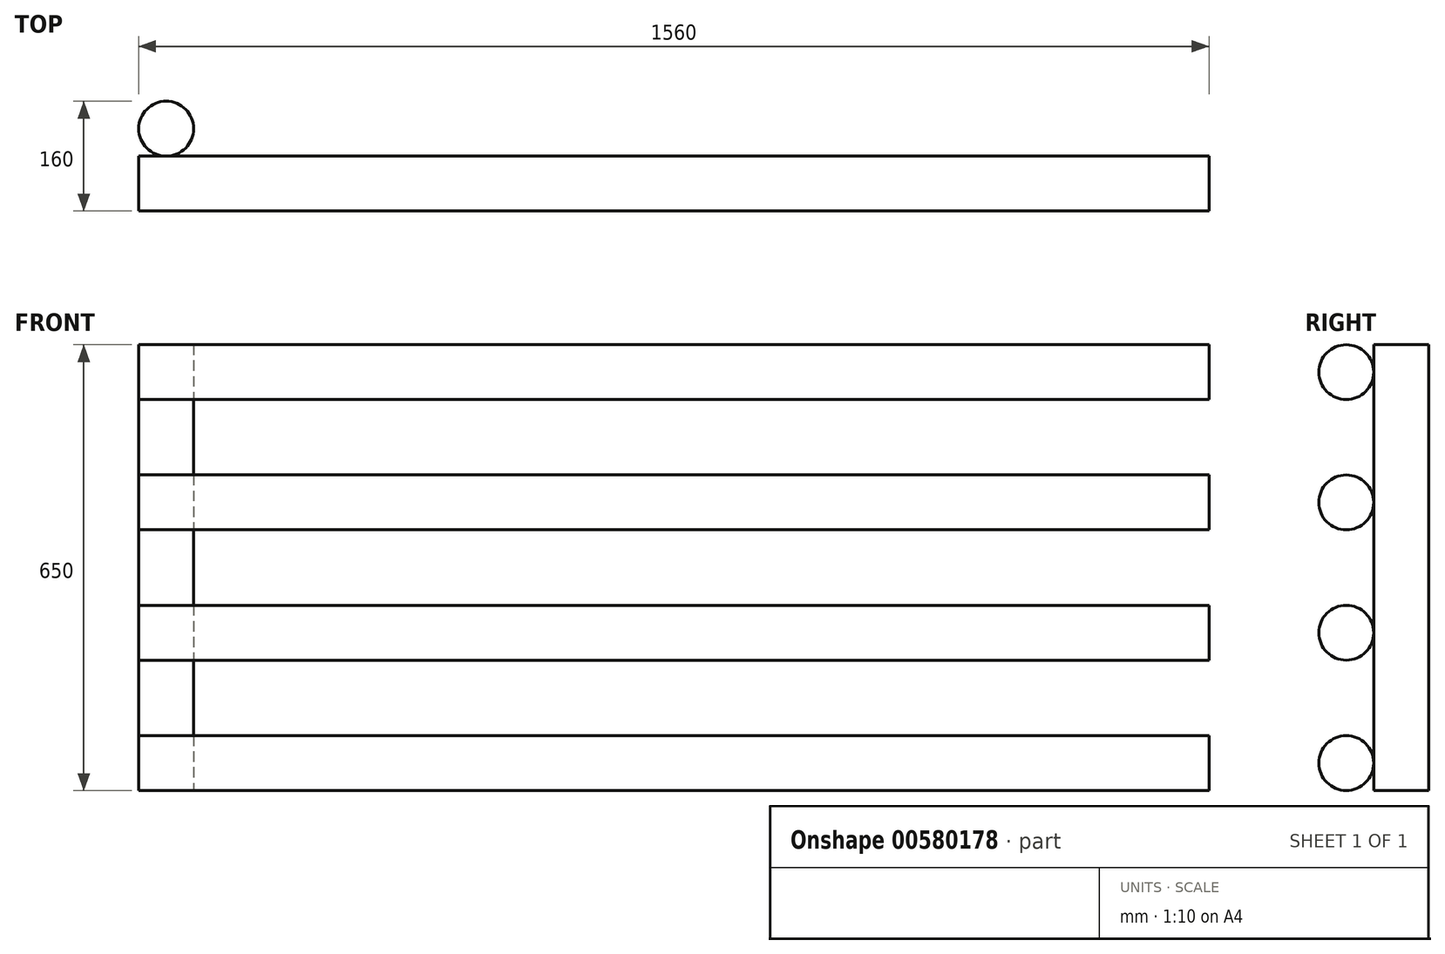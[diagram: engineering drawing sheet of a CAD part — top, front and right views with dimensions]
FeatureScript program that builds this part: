
annotation { "Feature Type Name" : "Feature", "Feature Type Description" : "" }
export const myFeature = defineFeature(function(context is Context, id is Id, definition is map)
    precondition{}
    {
        {
            var Q0;
            Q0=qCreatedBy(makeId("Right.planeOp"),FACE);
            var sketch = newSketch(context, id + "F0", { "sketchPlane" : qUnion([Q0])});
            skCircle(sketch, "E0", {"center": v(0, 0) * mm, "radius": 40 * mm});
            skCircle(sketch, "E1", {"center": v(0, 190) * mm, "radius": 40 * mm});
            skCircle(sketch, "E2", {"center": v(0, 380) * mm, "radius": 40 * mm});
            skCircle(sketch, "E3", {"center": v(0, 570) * mm, "radius": 40 * mm});
            skSolve(sketch);
        }
        {
            var Q0;
            Q0=makeQuery(id+"F0.imprint","IMPRINT",FACE,{"disambiguationData":[TD([[makeQuery(id+"F0.imprint","IMPRINT",EDGE,{"derivedFrom":sQuery(id+"F0.wireOp",EDGE,"E0")}),1.0]])]});
            var Q1;
            Q1=makeQuery(id+"F0.imprint","IMPRINT",FACE,{"disambiguationData":[TD([[makeQuery(id+"F0.imprint","IMPRINT",EDGE,{"derivedFrom":sQuery(id+"F0.wireOp",EDGE,"E3")}),1.0]])]});
            var Q2;
            Q2=makeQuery(id+"F0.imprint","IMPRINT",FACE,{"disambiguationData":[TD([[makeQuery(id+"F0.imprint","IMPRINT",EDGE,{"derivedFrom":sQuery(id+"F0.wireOp",EDGE,"E1")}),1.0]])]});
            var Q3;
            Q3=makeQuery(id+"F0.imprint","IMPRINT",FACE,{"disambiguationData":[TD([[makeQuery(id+"F0.imprint","IMPRINT",EDGE,{"derivedFrom":sQuery(id+"F0.wireOp",EDGE,"E2")}),1.0]])]});
            extrude(context, id + "F1", {"entities" : qUnion([Q0, Q1, Q2, Q3]), "depth" : 1560 * mm, "offsetDistance" : 25 * mm});
        }
        {
            var Q0;
            Q0=qCreatedBy(makeId("Top.planeOp"),FACE);
            var sketch = newSketch(context, id + "F2", { "sketchPlane" : qUnion([Q0])});
            skCircle(sketch, "E4", {"center": v(40, 80) * mm, "radius": 40 * mm});
            skPoint(sketch, "E5.center.orphan", {"position": v(0, 80) * mm});
            skSolve(sketch);
        }
        {
            var Q0;
            Q0=makeQuery(id+"F2.imprint","IMPRINT",FACE,{"disambiguationData":[TD([[makeQuery(id+"F2.imprint","IMPRINT",EDGE,{"derivedFrom":sQuery(id+"F2.wireOp",EDGE,"E4")}),1.0]])]});
            extrude(context, id + "F3", {"entities" : qUnion([Q0]), "depth" : 610 * mm, "offsetDistance" : 25 * mm, "hasSecondDirection" : true, "secondDirectionOppositeDirection" : true, "secondDirectionDepth" : 40 * mm});
        }
    });
